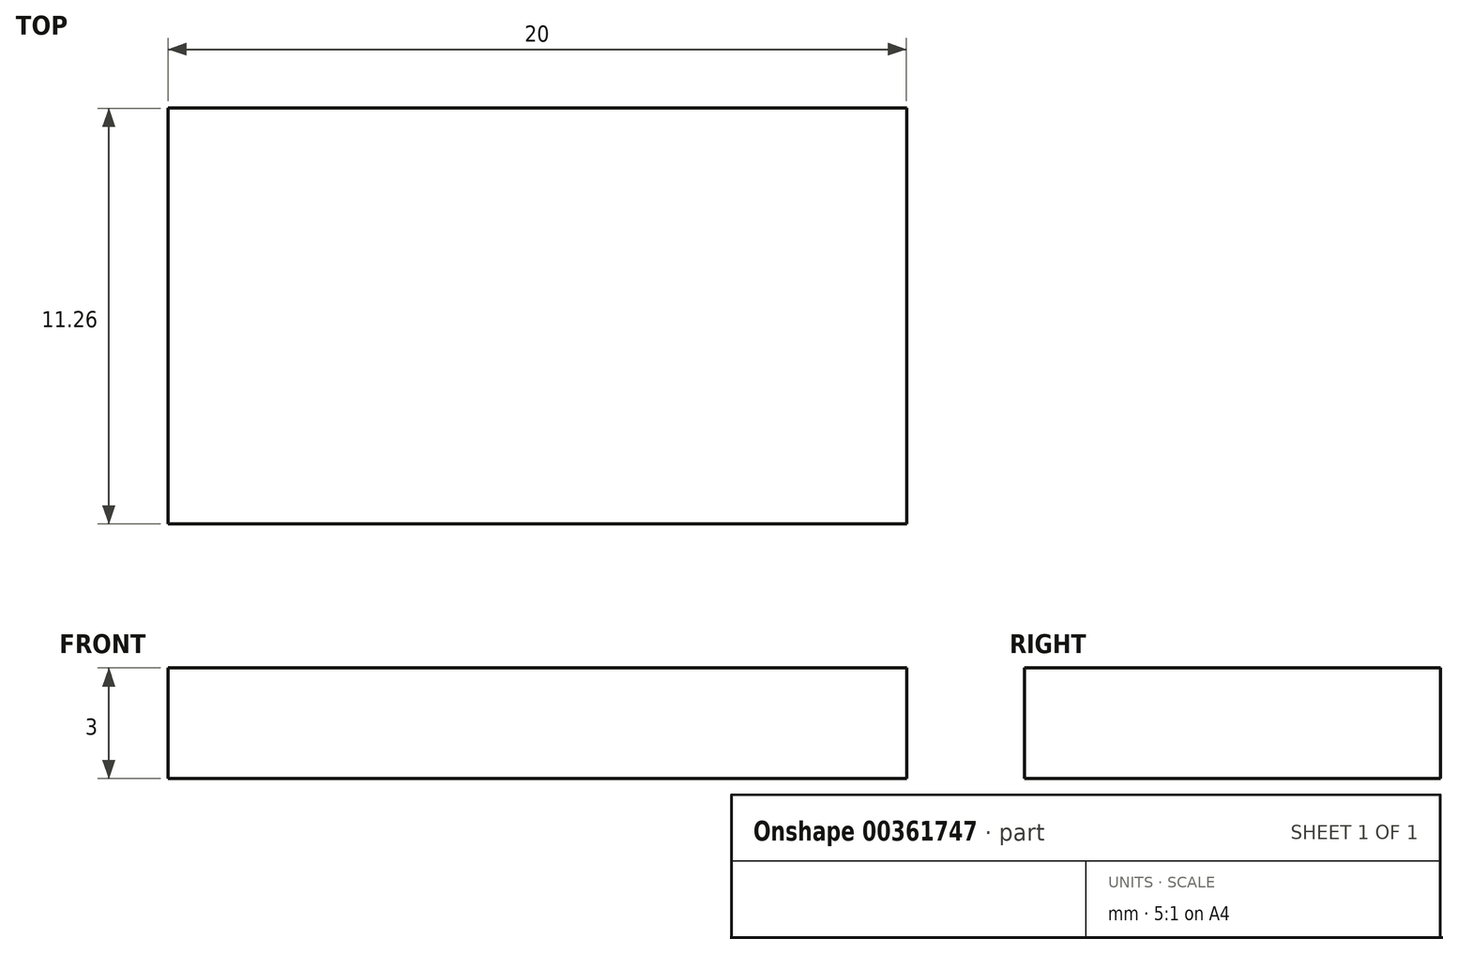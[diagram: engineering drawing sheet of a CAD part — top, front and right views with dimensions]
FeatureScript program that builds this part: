
annotation { "Feature Type Name" : "Feature", "Feature Type Description" : "" }
export const myFeature = defineFeature(function(context is Context, id is Id, definition is map)
    precondition{}
    {
        {
            var Q0;
            Q0=qCreatedBy(makeId("Top.planeOp"),FACE);
            var sketch = newSketch(context, id + "F0", { "sketchPlane" : qUnion([Q0])});
            skLineSegment(sketch, "E0.bottom", {"start": v(-61.4, 39.43) * mm, "end": v(-41.39, 39.43) * mm});
            skLineSegment(sketch, "E0.top", {"start": v(-61.4, 28.17) * mm, "end": v(-41.39, 28.17) * mm});
            skLineSegment(sketch, "E0.left", {"start": v(-61.4, 39.43) * mm, "end": v(-61.4, 28.17) * mm});
            skLineSegment(sketch, "E0.right", {"start": v(-41.39, 39.43) * mm, "end": v(-41.39, 28.17) * mm});
            skSolve(sketch);
        }
        {
            var Q0;
            Q0=makeQuery(id+"F0.imprint","IMPRINT",FACE,{"disambiguationData":[TD([[makeQuery(id+"F0.imprint","IMPRINT",EDGE,{"derivedFrom":sQuery(id+"F0.wireOp",EDGE,"E0.bottom")}),-1.0]])]});
            extrude(context, id + "F1", {"entities" : qUnion([Q0]), "depth" : 3 * mm});
        }
    });
